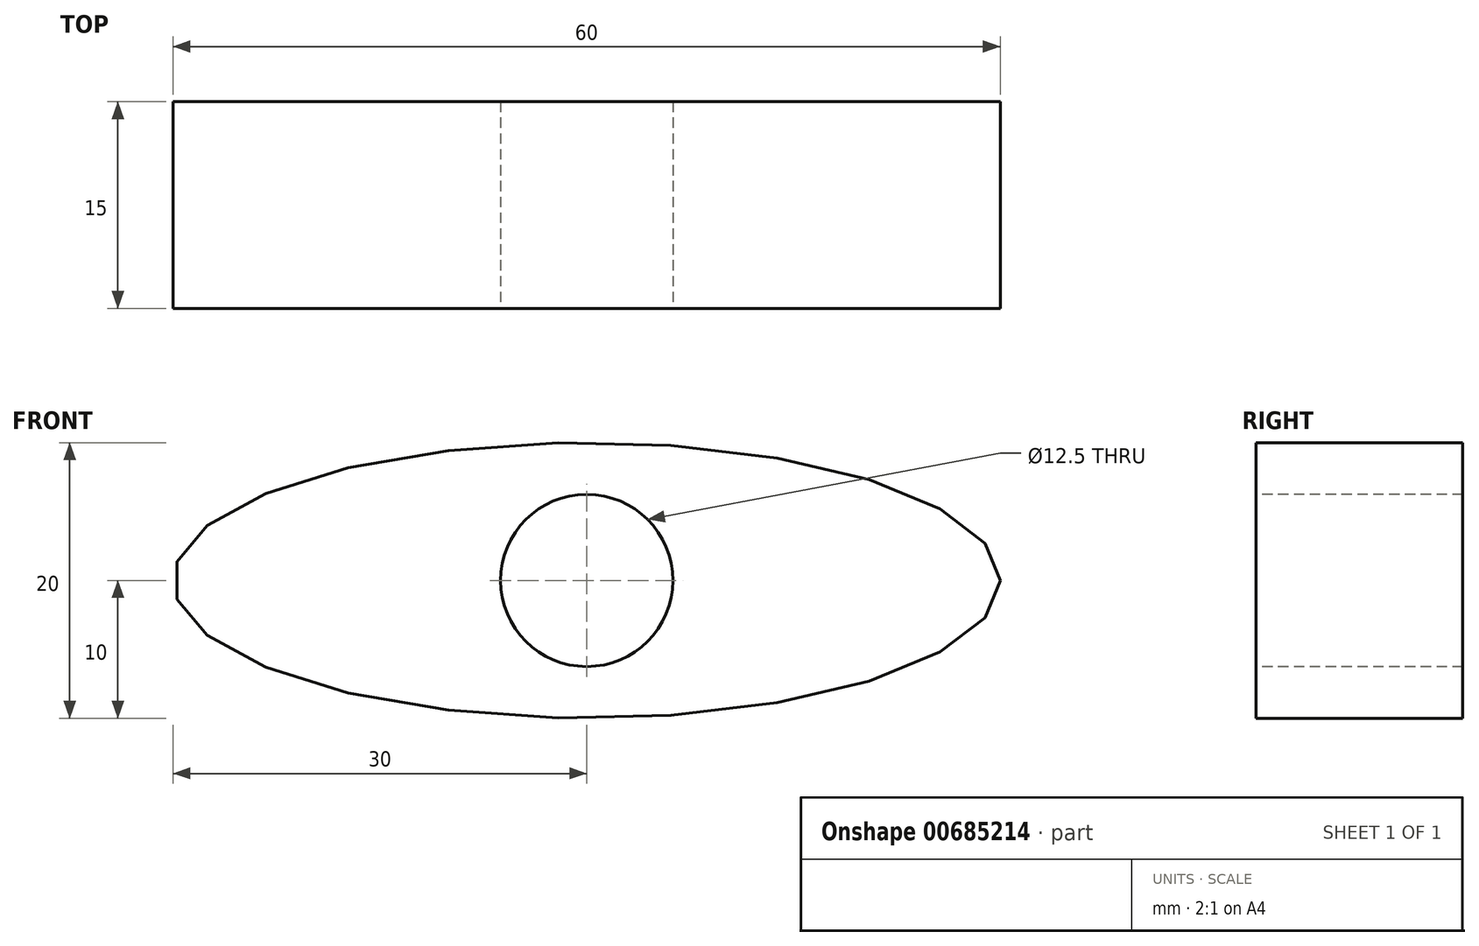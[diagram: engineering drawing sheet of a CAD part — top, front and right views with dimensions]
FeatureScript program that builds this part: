
annotation { "Feature Type Name" : "Feature", "Feature Type Description" : "" }
export const myFeature = defineFeature(function(context is Context, id is Id, definition is map)
    precondition{}
    {
        {
            var Q0;
            Q0=qCreatedBy(makeId("Front.planeOp"),FACE);
            var sketch = newSketch(context, id + "F0", { "sketchPlane" : qUnion([Q0])});
            skCircle(sketch, "E0", {"center": v(0, 0) * mm, "radius": 6.25 * mm});
            skCircle(sketch, "E1", {"center": v(0, 0) * mm, "radius": 1.25 * mm});
            skEllipse(sketch, "E2", {"center": v(0, 0) * mm, "majorRadius": 30 * mm, "minorRadius": 10 * mm, "majorAxis": v(1, 0)});
            skSolve(sketch);
        }
        {
            var Q0;
            Q0 = qSketchRegion(id + "F0", true);
            extrude(context, id + "F1", {"entities" : qUnion([Q0]), "oppositeDirection" : true, "depth" : 15 * mm, "offsetDistance" : 25 * mm});
        }
    });
